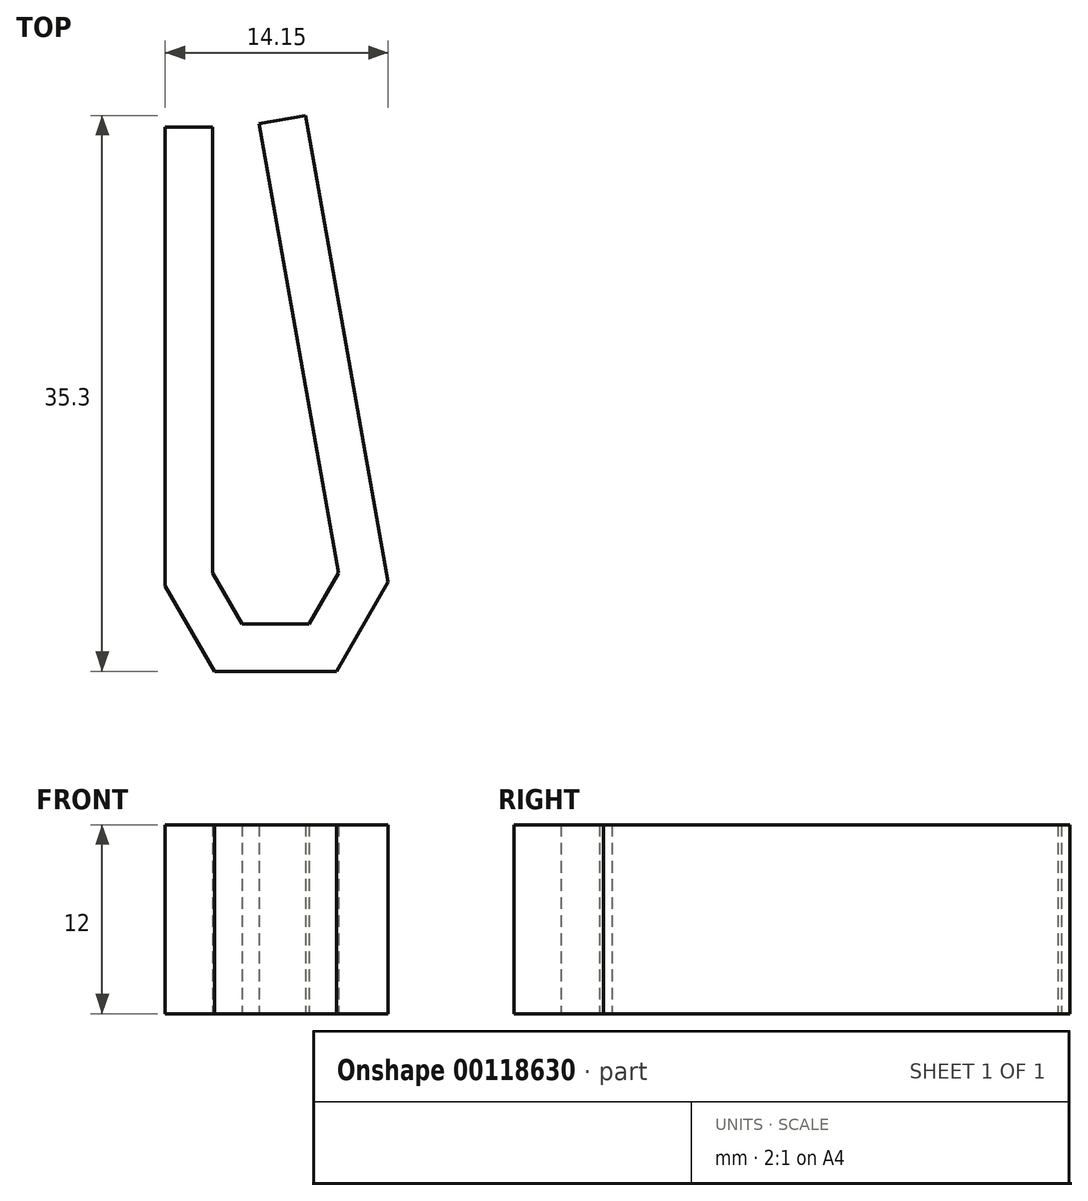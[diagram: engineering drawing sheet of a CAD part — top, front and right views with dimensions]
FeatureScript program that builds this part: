
annotation { "Feature Type Name" : "Feature", "Feature Type Description" : "" }
export const myFeature = defineFeature(function(context is Context, id is Id, definition is map)
    precondition{}
    {
        {
            var Q0;
            Q0=qCreatedBy(makeId("Top.planeOp"),FACE);
            var sketch = newSketch(context, id + "F0", { "sketchPlane" : qUnion([Q0])});
            skLineSegment(sketch, "E0", {"start": v(-12.98, 31.84) * mm, "end": v(-12.98, 3.51) * mm});
            skLineSegment(sketch, "E1", {"start": v(-12.98, 3.51) * mm, "end": v(-11.1, 0.28) * mm});
            skLineSegment(sketch, "E2", {"start": v(-11.1, 0.28) * mm, "end": v(-6.84, 0.28) * mm});
            skLineSegment(sketch, "E3", {"start": v(-6.84, 0.28) * mm, "end": v(-4.98, 3.51) * mm});
            skLineSegment(sketch, "E4", {"start": v(-4.98, 3.51) * mm, "end": v(-10, 32.06) * mm});
            skLineSegment(sketch, "E5", {"start": v(-10, 32.06) * mm, "end": v(-7.05, 32.58) * mm});
            skLineSegment(sketch, "E6", {"start": v(-7.05, 32.58) * mm, "end": v(-1.83, 2.96) * mm});
            skLineSegment(sketch, "E7", {"start": v(-1.83, 2.96) * mm, "end": v(-5.11, -2.72) * mm});
            skLineSegment(sketch, "E8", {"start": v(-5.11, -2.72) * mm, "end": v(-12.84, -2.72) * mm});
            skLineSegment(sketch, "E9", {"start": v(-12.84, -2.72) * mm, "end": v(-15.98, 2.7) * mm});
            skLineSegment(sketch, "E10", {"start": v(-15.98, 2.7) * mm, "end": v(-15.98, 31.84) * mm});
            skLineSegment(sketch, "E11", {"start": v(-15.98, 31.84) * mm, "end": v(-12.98, 31.84) * mm});
            skLineSegment(sketch, "E12", {"start": v(-12.98, 11.72) * mm, "end": v(-15.98, 11.72) * mm, "construction": true});
            skLineSegment(sketch, "E13", {"start": v(-8.4, -4.43) * mm, "end": v(-11, -5.93) * mm, "construction": true});
            skLineSegment(sketch, "E14", {"start": v(3.03, 0.28) * mm, "end": v(3.03, -2.72) * mm, "construction": true});
            skLineSegment(sketch, "E15", {"start": v(-4.8, 3.8) * mm, "end": v(-2.2, 2.3) * mm, "construction": true});
            skLineSegment(sketch, "E16", {"start": v(-5.3, 5.3) * mm, "end": v(-2.34, 5.83) * mm, "construction": true});
            skSolve(sketch);
        }
        {
            var Q0;
            Q0=makeQuery(id+"F0.imprint","IMPRINT",FACE,{"disambiguationData":[TD([[makeQuery(id+"F0.imprint","IMPRINT",EDGE,{"derivedFrom":sQuery(id+"F0.wireOp",EDGE,"E0")}),-1.0]])]});
            extrude(context, id + "F1", {"entities" : qUnion([Q0]), "depth" : 12 * mm});
        }
    });
